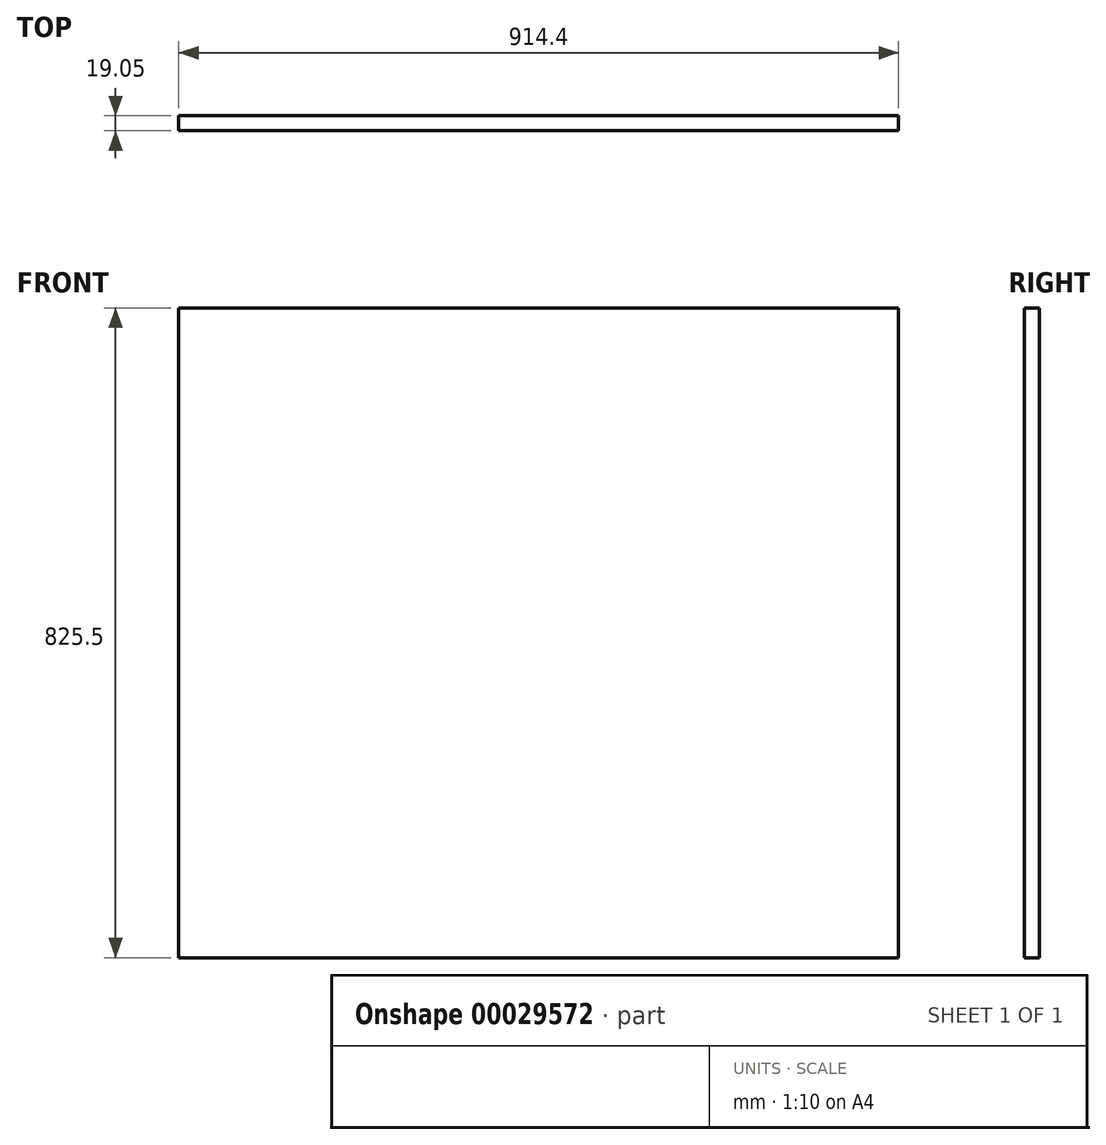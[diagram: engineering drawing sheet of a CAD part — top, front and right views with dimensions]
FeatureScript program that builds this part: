
annotation { "Feature Type Name" : "Feature", "Feature Type Description" : "" }
export const myFeature = defineFeature(function(context is Context, id is Id, definition is map)
    precondition{}
    {
        {
            var Q0;
            Q0=qCreatedBy(makeId("Front.planeOp"),FACE);
            var sketch = newSketch(context, id + "F0", { "sketchPlane" : qUnion([Q0])});
            skLineSegment(sketch, "E0.rect.bottom", {"start": v(457.2, 412.75) * mm, "end": v(-457.2, 412.75) * mm});
            skLineSegment(sketch, "E0.rect.top", {"start": v(457.2, -412.75) * mm, "end": v(-457.2, -412.75) * mm});
            skLineSegment(sketch, "E0.rect.left", {"start": v(457.2, 412.75) * mm, "end": v(457.2, -412.75) * mm});
            skLineSegment(sketch, "E0.rect.right", {"start": v(-457.2, 412.75) * mm, "end": v(-457.2, -412.75) * mm});
            skPoint(sketch, "E0.rect.middle", {"position": v(0, 0) * mm});
            skPoint(sketch, "E1", {"position": v(393.7, 0) * mm});
            skPoint(sketch, "E1.positionSnap0", {"position": v(457.2, 0) * mm});
            skSolve(sketch);
        }
        {
            var Q0;
            Q0=qSketchRegion(id+"F0",true);
            extrude(context, id + "F1", {"entities" : qUnion([Q0]), "depth" : 19.05 * mm});
        }
    });
